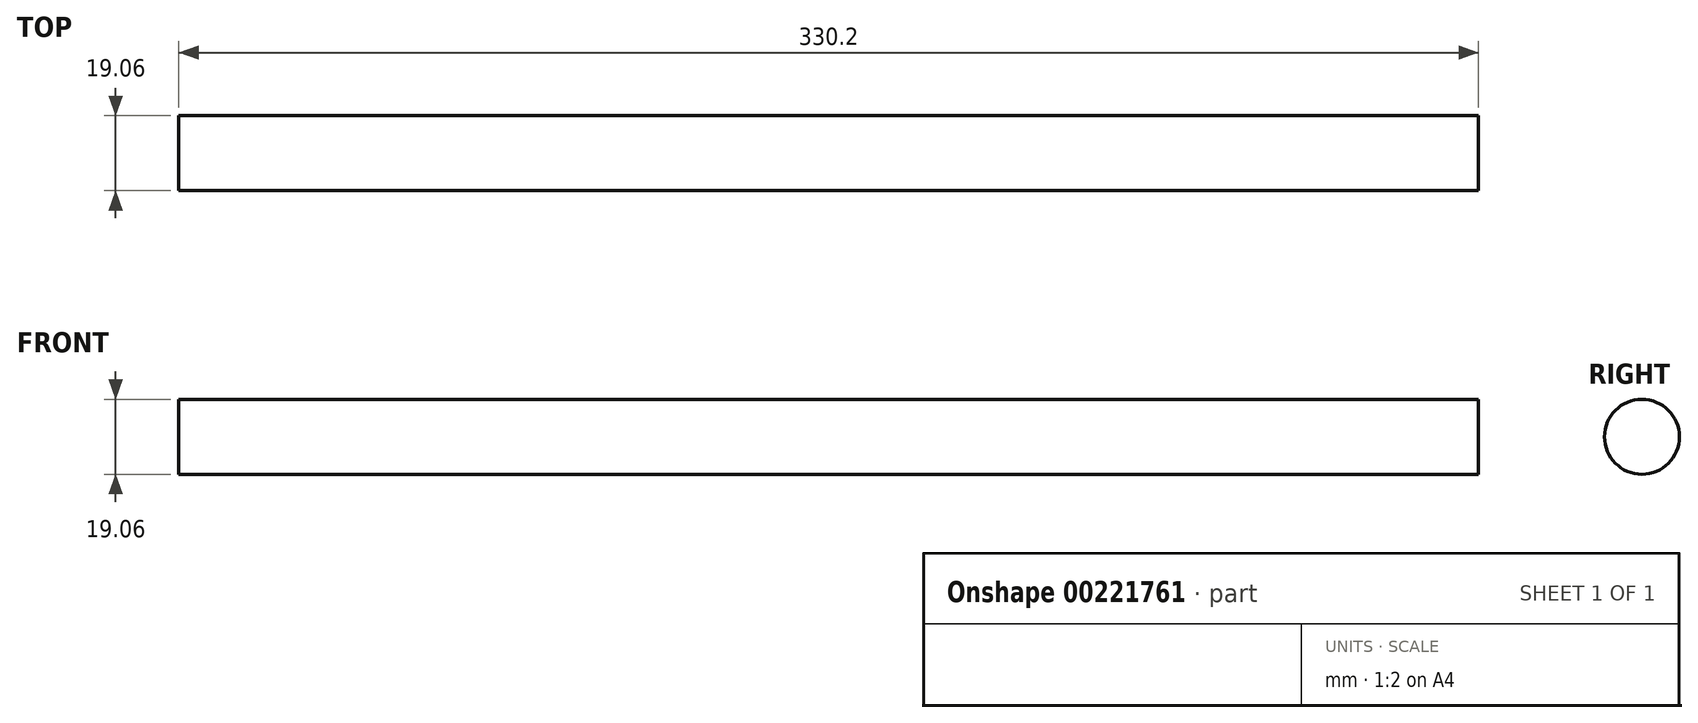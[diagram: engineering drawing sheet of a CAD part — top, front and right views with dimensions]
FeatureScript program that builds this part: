
annotation { "Feature Type Name" : "Feature", "Feature Type Description" : "" }
export const myFeature = defineFeature(function(context is Context, id is Id, definition is map)
    precondition{}
    {
        {
            var Q0;
            Q0=qCreatedBy(makeId("Right.planeOp"),FACE);
            var sketch = newSketch(context, id + "F0", { "sketchPlane" : qUnion([Q0])});
            skCircle(sketch, "E0", {"center": v(0, 0) * mm, "radius": 9.53 * mm});
            skSolve(sketch);
        }
        {
            var Q0;
            Q0 = qSketchRegion(id + "F0", true);
            extrude(context, id + "F1", {"entities" : qUnion([Q0]), "depth" : 330.2 * mm});
        }
    });
